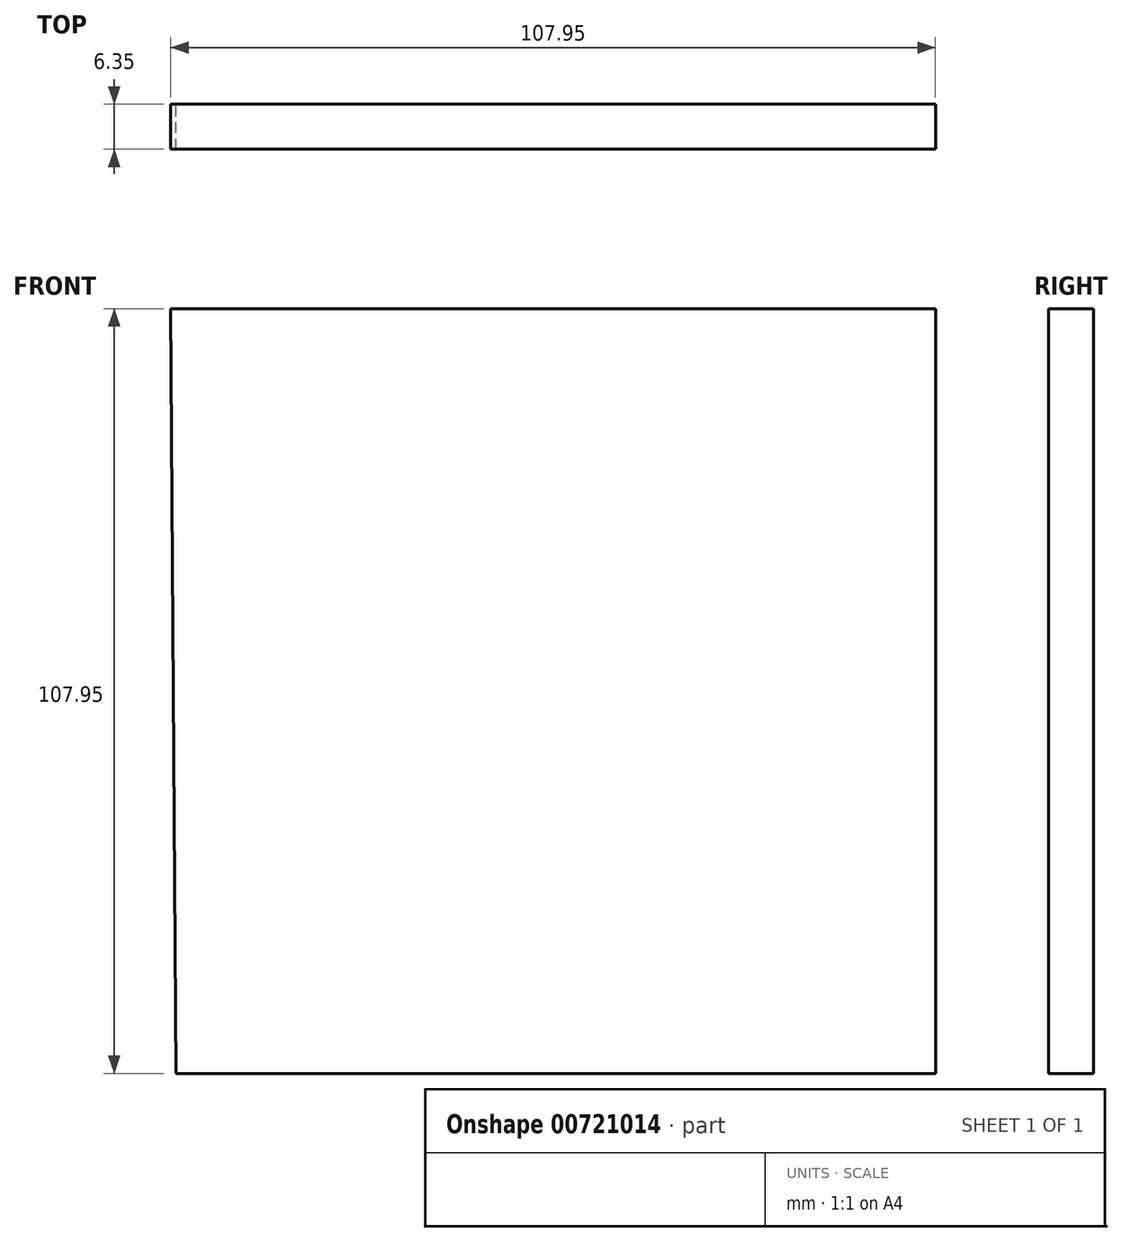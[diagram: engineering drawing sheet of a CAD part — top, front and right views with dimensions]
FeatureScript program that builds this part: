
annotation { "Feature Type Name" : "Feature", "Feature Type Description" : "" }
export const myFeature = defineFeature(function(context is Context, id is Id, definition is map)
    precondition{}
    {
        {
            var Q0;
            Q0=qCreatedBy(makeId("Front.planeOp"),FACE);
            var sketch = newSketch(context, id + "F0", { "sketchPlane" : qUnion([Q0])});
            skLineSegment(sketch, "E0", {"start": v(-37.32, 33.38) * mm, "end": v(70.63, 33.38) * mm});
            skLineSegment(sketch, "E1", {"start": v(70.63, 33.38) * mm, "end": v(70.63, -74.57) * mm});
            skLineSegment(sketch, "E2", {"start": v(70.63, -74.57) * mm, "end": v(-36.57, -74.57) * mm});
            skLineSegment(sketch, "E3", {"start": v(-36.57, -74.57) * mm, "end": v(-37.32, 33.38) * mm});
            skSolve(sketch);
        }
        {
            var Q0;
            Q0 = qSketchRegion(id + "F0", true);
            extrude(context, id + "F1", {"entities" : qUnion([Q0]), "depth" : 6.35 * mm, "offsetDistance" : 25.4 * mm});
        }
    });
